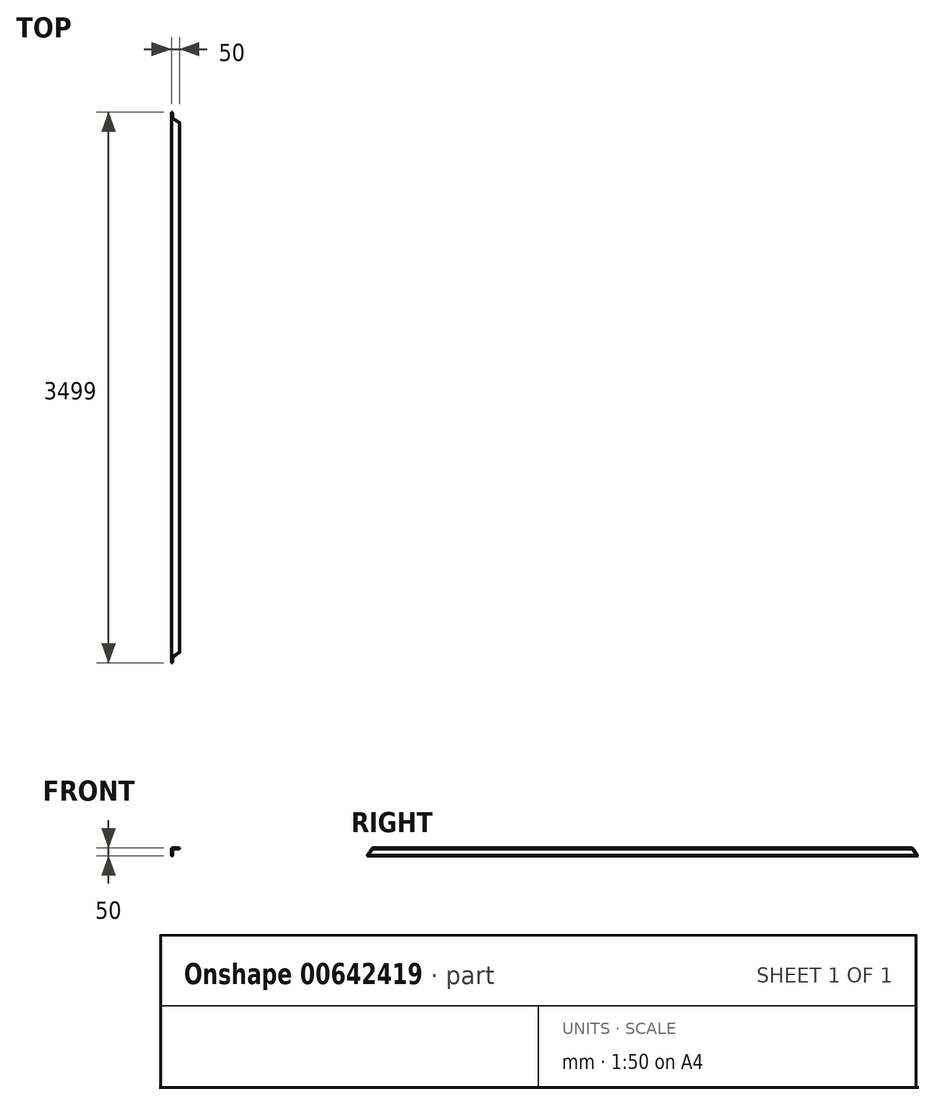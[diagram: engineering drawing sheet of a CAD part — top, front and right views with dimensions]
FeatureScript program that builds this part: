
annotation { "Feature Type Name" : "Feature", "Feature Type Description" : "" }
export const myFeature = defineFeature(function(context is Context, id is Id, definition is map)
    precondition{}
    {
        {
            var Q0;
            Q0=qCreatedBy(makeId("Front.planeOp"),FACE);
            var sketch = newSketch(context, id + "F0", { "sketchPlane" : qUnion([Q0])});
            skLineSegment(sketch, "E0", {"start": v(0, 0) * mm, "end": v(0, 50) * mm});
            skLineSegment(sketch, "E1", {"start": v(0, 50) * mm, "end": v(50, 50) * mm});
            skLineSegment(sketch, "E2.0", {"start": v(13, 44) * mm, "end": v(46.5, 44) * mm});
            skLineSegment(sketch, "E2.1", {"start": v(6, 3.5) * mm, "end": v(6, 37) * mm});
            skPoint(sketch, "E3.visualSharp", {"position": v(6, 44) * mm});
            skArc(sketch, "E3.filletArc", {"start": v(13, 44) * mm, "mid": v(8.05, 41.95) * mm, "end": v(6, 37) * mm});
            skLineSegment(sketch, "E4", {"start": v(50, 50) * mm, "end": v(50, 47.5) * mm});
            skLineSegment(sketch, "E5", {"start": v(0, 0) * mm, "end": v(2.5, 0) * mm});
            skPoint(sketch, "E6.visualSharp", {"position": v(50, 44) * mm});
            skArc(sketch, "E6.filletArc", {"start": v(46.5, 44) * mm, "mid": v(48.97, 45.03) * mm, "end": v(50, 47.5) * mm});
            skPoint(sketch, "E7.visualSharp", {"position": v(6, 0) * mm});
            skArc(sketch, "E7.filletArc", {"start": v(2.5, 0) * mm, "mid": v(4.97, 1.03) * mm, "end": v(6, 3.5) * mm});
            skSolve(sketch);
        }
        {
            var Q0;
            Q0=makeQuery(id+"F0.imprint","IMPRINT",FACE,{"disambiguationData":[TD([[makeQuery(id+"F0.imprint","IMPRINT",EDGE,{"derivedFrom":sQuery(id+"F0.wireOp",EDGE,"E0")}),-1.0]])]});
            extrude(context, id + "F1", {"entities" : qUnion([Q0]), "depth" : 3500 * mm, "offsetDistance" : 25 * mm});
        }
        {
            var Q0;
            Q0=makeQuery(id+"F1.opExtrude","CAP_EDGE",EDGE,{"disambiguationData":[OSD([sQuery(id+"F0.wireOp",EDGE,"E6.filletArc")])],"isStart":false});
            cPoint(context, id + "F2", {"entities" : qUnion([Q0]), "parameter" : 0.5});
        }
        {
            var Q0;
            Q0=makeQuery(id+"F1.opExtrude","CAP_EDGE",EDGE,{"disambiguationData":[OSD([sQuery(id+"F0.wireOp",EDGE,"E7.filletArc")])],"isStart":false});
            cPoint(context, id + "F3", {"entities" : qUnion([Q0]), "parameter" : 0.5});
        }
        {
            var Q0;
            Q0=makeQuery(id+"F1.opExtrude","CAP_EDGE",EDGE,{"disambiguationData":[OSD([sQuery(id+"F0.wireOp",EDGE,"E6.filletArc")])],"isStart":true});
            cPoint(context, id + "F4", {"entities" : qUnion([Q0]), "parameter" : 0.5});
        }
        {
            var Q0;
            Q0 = qCreatedBy(id + "F2" ,VERTEX);
            var Q1;
            Q1 = qCreatedBy(id + "F3" ,VERTEX);
            var Q2;
            Q2 = qCreatedBy(id + "F4" ,VERTEX);
            cPlane(context, id + "F5", {"entities" : qUnion([Q0, Q1, Q2]), "cplaneType" : CPlaneType.THREE_POINT, "offset" : 25 * mm, "width" : 150 * mm, "height" : 150 * mm});
        }
        {
            var Q0;
            Q0=qCreatedBy(id+"F5.planeOp",FACE);
            var sketch = newSketch(context, id + "F6", { "sketchPlane" : qUnion([Q0])});
            skPoint(sketch, "E8.0", {"position": v(3500, 0) * mm});
            skLineSegment(sketch, "E9", {"start": v(3500, 0) * mm, "end": v(3429.29, 70.71) * mm});
            skLineSegment(sketch, "E10", {"start": v(3500, 0) * mm, "end": v(3500, 104.4) * mm, "construction": true});
            skLineSegment(sketch, "E11", {"start": v(3429.29, 70.71) * mm, "end": v(3500, 70.71) * mm});
            skLineSegment(sketch, "E12", {"start": v(3500, 70.71) * mm, "end": v(3500, 0) * mm});
            skSolve(sketch);
        }
        {
            var Q0;
            Q0=makeQuery(id+"F6.imprint","IMPRINT",FACE,{"disambiguationData":[TD([[makeQuery(id+"F6.imprint","IMPRINT",EDGE,{"derivedFrom":sQuery(id+"F6.wireOp",EDGE,"E9")}),-1.0]])]});
            extrude(context, id + "F7", {"entities" : qUnion([Q0]), "operationType" : NewBodyOperationType.REMOVE, "depth" : 45 * mm, "offsetDistance" : 25 * mm});
        }
        {
            var Q0;
            Q0=qCreatedBy(id+"F5.planeOp",FACE);
            var sketch = newSketch(context, id + "F8", { "sketchPlane" : qUnion([Q0])});
            skLineSegment(sketch, "E13.0", {"start": v(3500, 0) * mm, "end": v(0, 0) * mm});
            skLineSegment(sketch, "E14", {"start": v(0, 0) * mm, "end": v(70.71, 70.71) * mm});
            skLineSegment(sketch, "E15", {"start": v(70.71, 70.71) * mm, "end": v(0, 70.71) * mm});
            skLineSegment(sketch, "E16", {"start": v(0, 70.71) * mm, "end": v(0, 0) * mm});
            skSolve(sketch);
        }
        {
            var Q0;
            Q0=makeQuery(id+"F8.imprint","IMPRINT",FACE,{"disambiguationData":[TD([[makeQuery(id+"F8.imprint","IMPRINT",EDGE,{"derivedFrom":sQuery(id+"F8.wireOp",EDGE,"E14")}),1.0]])]});
            extrude(context, id + "F9", {"entities" : qUnion([Q0]), "operationType" : NewBodyOperationType.REMOVE, "depth" : 45 * mm, "offsetDistance" : 25 * mm});
        }
        {
            var Q0;
            Q0=qCreatedBy(makeId("Front.planeOp"),FACE);
            var sketch = newSketch(context, id + "F10", { "sketchPlane" : qUnion([Q0])});
            skPoint(sketch, "E17.0", {"position": v(48.97, 45.03) * mm});
            skPoint(sketch, "E18.0", {"position": v(4.97, 1.03) * mm});
            skPoint(sketch, "E19.0", {"position": v(50, 50) * mm});
            skLineSegment(sketch, "E20.0", {"start": v(1.97, -1.97) * mm, "end": v(51.97, 48.03) * mm});
            skLineSegment(sketch, "E21.0", {"start": v(1.62, -1.62) * mm, "end": v(51.62, 48.38) * mm});
            skLineSegment(sketch, "E22", {"start": v(51.62, 48.38) * mm, "end": v(51.97, 48.03) * mm});
            skLineSegment(sketch, "E23", {"start": v(1.62, -1.62) * mm, "end": v(1.97, -1.97) * mm});
            skSolve(sketch);
        }
        {
            var Q0;
            Q0=makeQuery(id+"F10.imprint","IMPRINT",FACE,{"disambiguationData":[TD([[makeQuery(id+"F10.imprint","IMPRINT",EDGE,{"derivedFrom":sQuery(id+"F10.wireOp",EDGE,"E20.0")}),1.0]])]});
            extrude(context, id + "F11", {"entities" : qUnion([Q0]), "operationType" : NewBodyOperationType.REMOVE, "endBound" : BoundingType.THROUGH_ALL, "depth" : 25 * mm, "offsetDistance" : 25 * mm});
        }
        {
            var Q0;
            Q0=makeQuery(id+"F1.opExtrude","SWEPT_EDGE",EDGE,{"disambiguationData":[OSD([sQuery(id+"F0.wireOp",EDGE,"E0"),sQuery(id+"F0.wireOp",EDGE,"E5")])]});
            var Q1;
            Q1=qCreatedBy(id+"F5.planeOp",FACE);
            cPlane(context, id + "F12", {"entities" : qUnion([Q0, Q1]), "cplaneType" : CPlaneType.LINE_ANGLE, "offset" : 25 * mm, "angle" : 90 * degree, "width" : 150 * mm, "height" : 150 * mm});
        }
        {
            var Q0;
            Q0=qCreatedBy(id+"F12.planeOp",FACE);
            var sketch = newSketch(context, id + "F13", { "sketchPlane" : qUnion([Q0])});
            skPoint(sketch, "E24.0", {"position": v(0, 3500) * mm});
            skLineSegment(sketch, "E25.bottom", {"start": v(3502.19, 2.38) * mm, "end": v(-9, 2.38) * mm});
            skLineSegment(sketch, "E25.top", {"start": v(3502.19, -5) * mm, "end": v(-9, -5) * mm});
            skLineSegment(sketch, "E25.left", {"start": v(3502.19, 2.38) * mm, "end": v(3502.19, -5) * mm});
            skLineSegment(sketch, "E25.right", {"start": v(-9, 2.38) * mm, "end": v(-9, -5) * mm});
            skSolve(sketch);
        }
        {
            var Q0;
            Q0=makeQuery(id+"F13.imprint","IMPRINT",FACE,{"disambiguationData":[TD([[makeQuery(id+"F13.imprint","IMPRINT",EDGE,{"derivedFrom":sQuery(id+"F13.wireOp",EDGE,"E25.bottom")}),1.0]])]});
            extrude(context, id + "F14", {"entities" : qUnion([Q0]), "operationType" : NewBodyOperationType.REMOVE, "oppositeDirection" : true, "depth" : 0.5 * mm, "offsetDistance" : 25 * mm});
        }
    });
